# Revit family: KS Polar plus Gleitlager U140, Ø355,6
name_source: partatom
category: Allgemeines Modell
revit_build: Autodesk Revit 2017 (Build: 20190507_1515(x64)
units: mm (PartAtom-declared; Revit-internal decimal feet)

## family parameters
Arbeitsebenenbasiert = Ja
Beim Laden mit Abzugskörper schneiden = Nein
Bemaßung runder Anschluss = Durchmesser verwenden
Gemeinsam genutzt = Ja
Immer vertikal = Nein
Kann Basisbauteil für Bewehrung sein = Nein
Raumberechnungspunkt = Nein
Teiletyp = Normal

## types (1)
- Polar plus, Gleitlager U140, Ø355,6
    Artikelnummer = 74742356
    Bauart = U-Lager
    Breite = 498 mm  [stored 1.63386 ft]
    Breite Material = 60 mm
    Breite Unterbau = 140 mm
    EAN = 4250928443052
    Fabrikat = MEFA
    Firma = MEFA Befestigungs- und Montagesysteme GmbH
    Gewicht = 12.29 kg
    Gewicht pro Bauteil = 12.29 kg
    Höhe Sohle = 98 mm
    Höhe Unterbau = 60 mm
    Kurztext1 = Gleitlager U Polar Plus
    Kurztext2 = 355.6 mm Iso 40 x 226 mm
    L1 = 3 mm  [stored 0.00984252 ft]
    L2 = 269 mm
    Lochabstand längs = 0 mm  [stored 0 ft]
    Länge = 0 mm  [stored 0 ft]
    Länge Schale = 226 mm
    Länge Unterbau = 220 mm
    Material = Stahl
    Materialname = S235
    Mengeneinheit = St
    Oberflaeche = galvanisch verzinkt
    Rohraußendurchmesser = 356 mm
    Sicherheitsfaktor = 0
    Stärke = 0 mm  [stored 0 ft]
    Stärke Material = 6 mm  [stored 0.019685 ft]
    Vorgabe-Ansicht = 1219 mm
    max. zul. Last hängend = 0.00 kN
    vpe = 1 St

note: [stored X ft] marks values corroborated as IEEE doubles in the binary element streams (Revit-internal decimal feet)

## geometry (parser evidence)
native form markers: Sweep x1
no freeform markers — native parametric forms only
